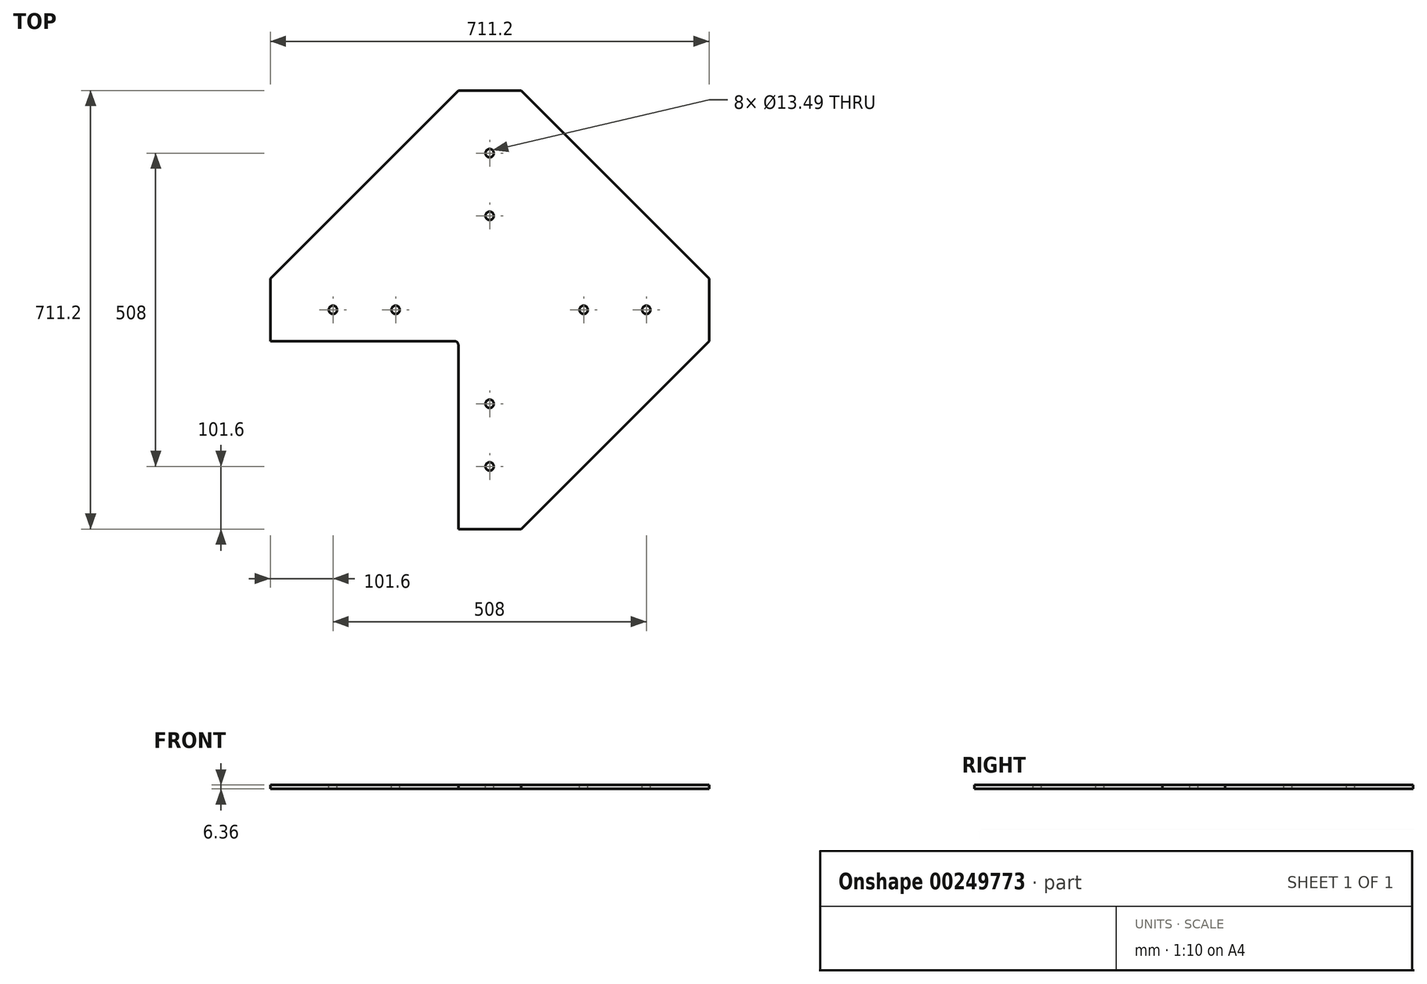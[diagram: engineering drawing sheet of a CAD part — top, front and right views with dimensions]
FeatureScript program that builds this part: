
annotation { "Feature Type Name" : "Feature", "Feature Type Description" : "" }
export const myFeature = defineFeature(function(context is Context, id is Id, definition is map)
    precondition{}
    {
        {
            var Q0;
            Q0=qCreatedBy(makeId("Top.planeOp"),FACE);
            var sketch = newSketch(context, id + "F0", { "sketchPlane" : qUnion([Q0])});
            skLineSegment(sketch, "E0", {"start": v(-355.6, -50.8) * mm, "end": v(-355.6, 50.8) * mm});
            skLineSegment(sketch, "E1", {"start": v(-355.6, 50.8) * mm, "end": v(-50.8, 355.6) * mm});
            skLineSegment(sketch, "E2", {"start": v(-50.8, 355.6) * mm, "end": v(50.8, 355.6) * mm});
            skLineSegment(sketch, "E3", {"start": v(50.8, 355.6) * mm, "end": v(355.6, 50.8) * mm});
            skLineSegment(sketch, "E4", {"start": v(355.6, 50.8) * mm, "end": v(355.6, -50.8) * mm});
            skLineSegment(sketch, "E5", {"start": v(355.6, -50.8) * mm, "end": v(50.8, -355.6) * mm});
            skLineSegment(sketch, "E6", {"start": v(50.8, -355.6) * mm, "end": v(-50.8, -355.6) * mm});
            skLineSegment(sketch, "E7", {"start": v(-50.8, -355.6) * mm, "end": v(-355.6, -50.8) * mm, "construction": true});
            skLineSegment(sketch, "E8", {"start": v(-355.6, 0) * mm, "end": v(355.6, 0) * mm, "construction": true});
            skLineSegment(sketch, "E9", {"start": v(0, 355.6) * mm, "end": v(0, -355.6) * mm, "construction": true});
            skLineSegment(sketch, "E10", {"start": v(-50.8, -355.6) * mm, "end": v(-50.8, -50.8) * mm});
            skLineSegment(sketch, "E11", {"start": v(-50.8, -50.8) * mm, "end": v(-355.6, -50.8) * mm});
            skSolve(sketch);
        }
        {
            var Q0;
            Q0=makeQuery(id+"F0.imprint","IMPRINT",FACE,{"disambiguationData":[TD([[makeQuery(id+"F0.imprint","IMPRINT",EDGE,{"derivedFrom":sQuery(id+"F0.wireOp",EDGE,"E0")}),-1.0]])]});
            extrude(context, id + "F1", {"entities" : qUnion([Q0]), "endBound" : BoundingType.SYMMETRIC, "depth" : 6.35 * mm});
        }
        {
            var Q0;
            Q0=makeQuery(id+"F1.opExtrude","SWEPT_EDGE",EDGE,{"disambiguationData":[OSD([sQuery(id+"F0.wireOp",EDGE,"E10"),sQuery(id+"F0.wireOp",EDGE,"E11")])]});
            fillet(context, id + "F2", {"entities" : qUnion([Q0]), "radius" : 6.35 * mm, "tangentPropagation" : true, "allowEdgeOverflow" : false});
        }
        {
            var Q0;
            Q0=qCreatedBy(makeId("Top.planeOp"),FACE);
            var sketch = newSketch(context, id + "F3", { "sketchPlane" : qUnion([Q0])});
            skLineSegment(sketch, "E12.bottom", {"start": v(-50.8, 50.8) * mm, "end": v(50.8, 50.8) * mm});
            skLineSegment(sketch, "E12.top", {"start": v(-50.8, -50.8) * mm, "end": v(50.8, -50.8) * mm});
            skLineSegment(sketch, "E12.left", {"start": v(-50.8, 50.8) * mm, "end": v(-50.8, -50.8) * mm});
            skLineSegment(sketch, "E12.right", {"start": v(50.8, 50.8) * mm, "end": v(50.8, -50.8) * mm});
            skPoint(sketch, "E12.middle", {"position": v(0, 0) * mm});
            skSolve(sketch);
        }
        {
            var Q0;
            Q0=makeQuery(id+"F1.opExtrude","CAP_FACE",FACE,{"disambiguationData":[OSD([sQuery(id+"F0.wireOp",EDGE,"E0"),sQuery(id+"F0.wireOp",EDGE,"E1"),sQuery(id+"F0.wireOp",EDGE,"E2"),sQuery(id+"F0.wireOp",EDGE,"E3"),sQuery(id+"F0.wireOp",EDGE,"E4"),sQuery(id+"F0.wireOp",EDGE,"E5"),sQuery(id+"F0.wireOp",EDGE,"E6"),sQuery(id+"F0.wireOp",EDGE,"E10"),sQuery(id+"F0.wireOp",EDGE,"E11")])],"isStart":false});
            var sketch = newSketch(context, id + "F4", { "sketchPlane" : qUnion([Q0])});
            skLineSegment(sketch, "E13", {"start": v(0, -355.6) * mm, "end": v(0, -254) * mm});
            skPoint(sketch, "E13.endSnap0", {"position": v(0, -355.6) * mm});
            skLineSegment(sketch, "E14", {"start": v(0, -254) * mm, "end": v(0, -152.4) * mm});
            skLineSegment(sketch, "E15", {"start": v(0, -152.4) * mm, "end": v(0, -50.8) * mm});
            skPoint(sketch, "E16", {"position": v(0, 0) * mm});
            skLineSegment(sketch, "E17.1.0", {"start": v(152.4, 0) * mm, "end": v(50.8, 0) * mm});
            skLineSegment(sketch, "E17.1.1", {"start": v(254, 0) * mm, "end": v(152.4, 0) * mm});
            skLineSegment(sketch, "E17.1.2", {"start": v(355.6, 0) * mm, "end": v(254, 0) * mm});
            skLineSegment(sketch, "E17.2.0", {"start": v(0, 152.4) * mm, "end": v(0, 50.8) * mm});
            skLineSegment(sketch, "E17.2.1", {"start": v(0, 254) * mm, "end": v(0, 152.4) * mm});
            skLineSegment(sketch, "E17.2.2", {"start": v(0, 355.6) * mm, "end": v(0, 254) * mm});
            skLineSegment(sketch, "E17.3.0", {"start": v(-152.4, 0) * mm, "end": v(-50.8, 0) * mm});
            skLineSegment(sketch, "E17.3.1", {"start": v(-254, 0) * mm, "end": v(-152.4, 0) * mm});
            skLineSegment(sketch, "E17.3.2", {"start": v(-355.6, 0) * mm, "end": v(-254, 0) * mm});
            skLineSegment(sketch, "E17.anchor1", {"start": v(0, 0) * mm, "end": v(0, -355.6) * mm, "construction": true});
            skLineSegment(sketch, "E17.anchor2", {"start": v(0, 0) * mm, "end": v(-355.6, 0) * mm, "construction": true});
            skSolve(sketch);
        }
        {
            var Q0;
            Q0=sQuery(id+"F4.wireOp",VERTEX,"E14.start");
            var Q1;
            Q1=sQuery(id+"F4.wireOp",VERTEX,"E15.start");
            var Q2;
            Q2=sQuery(id+"F4.wireOp",VERTEX,"E17.1.1.end");
            var Q3;
            Q3=sQuery(id+"F4.wireOp",VERTEX,"E17.1.2.end");
            var Q4;
            Q4=sQuery(id+"F4.wireOp",VERTEX,"E17.2.0.start");
            var Q5;
            Q5=sQuery(id+"F4.wireOp",VERTEX,"E17.2.1.start");
            var Q6;
            Q6=sQuery(id+"F4.wireOp",VERTEX,"E17.3.1.end");
            var Q7;
            Q7=sQuery(id+"F4.wireOp",VERTEX,"E17.3.2.end");
            var Q8;
            Q8=makeQuery(id+"F1.opExtrude","SWEPT_BODY",BODY,{"disambiguationData":[OSD([sQuery(id+"F0.wireOp",EDGE,"E0"),sQuery(id+"F0.wireOp",EDGE,"E1"),sQuery(id+"F0.wireOp",EDGE,"E2"),sQuery(id+"F0.wireOp",EDGE,"E3"),sQuery(id+"F0.wireOp",EDGE,"E4"),sQuery(id+"F0.wireOp",EDGE,"E5"),sQuery(id+"F0.wireOp",EDGE,"E6"),sQuery(id+"F0.wireOp",EDGE,"E10"),sQuery(id+"F0.wireOp",EDGE,"E11")])]});
            hole(context, id + "F5", {"style" : HoleStyle.SIMPLE, "endStyle" : HoleEndStyle.THROUGH, "standardTappedOrClearance" : lookupTablePath({ "standard" : "ANSI", "fit" : "Normal (ASME)", "size" : "1/2", "type" : "Clearance" }), "standardBlindInLast" : lookupTablePath({ "fit" : "Free", "standard" : "ANSI", "size" : "1/2", "type" : "Clearance" }), "holeDiameter" : 13.5 * mm, "tappedDepth" : 12.7 * mm, "tapClearance" : 3, "locations" : qUnion([Q0, Q1, Q2, Q3, Q4, Q5, Q6, Q7]), "scope" : qUnion([Q8])});
        }
    });
